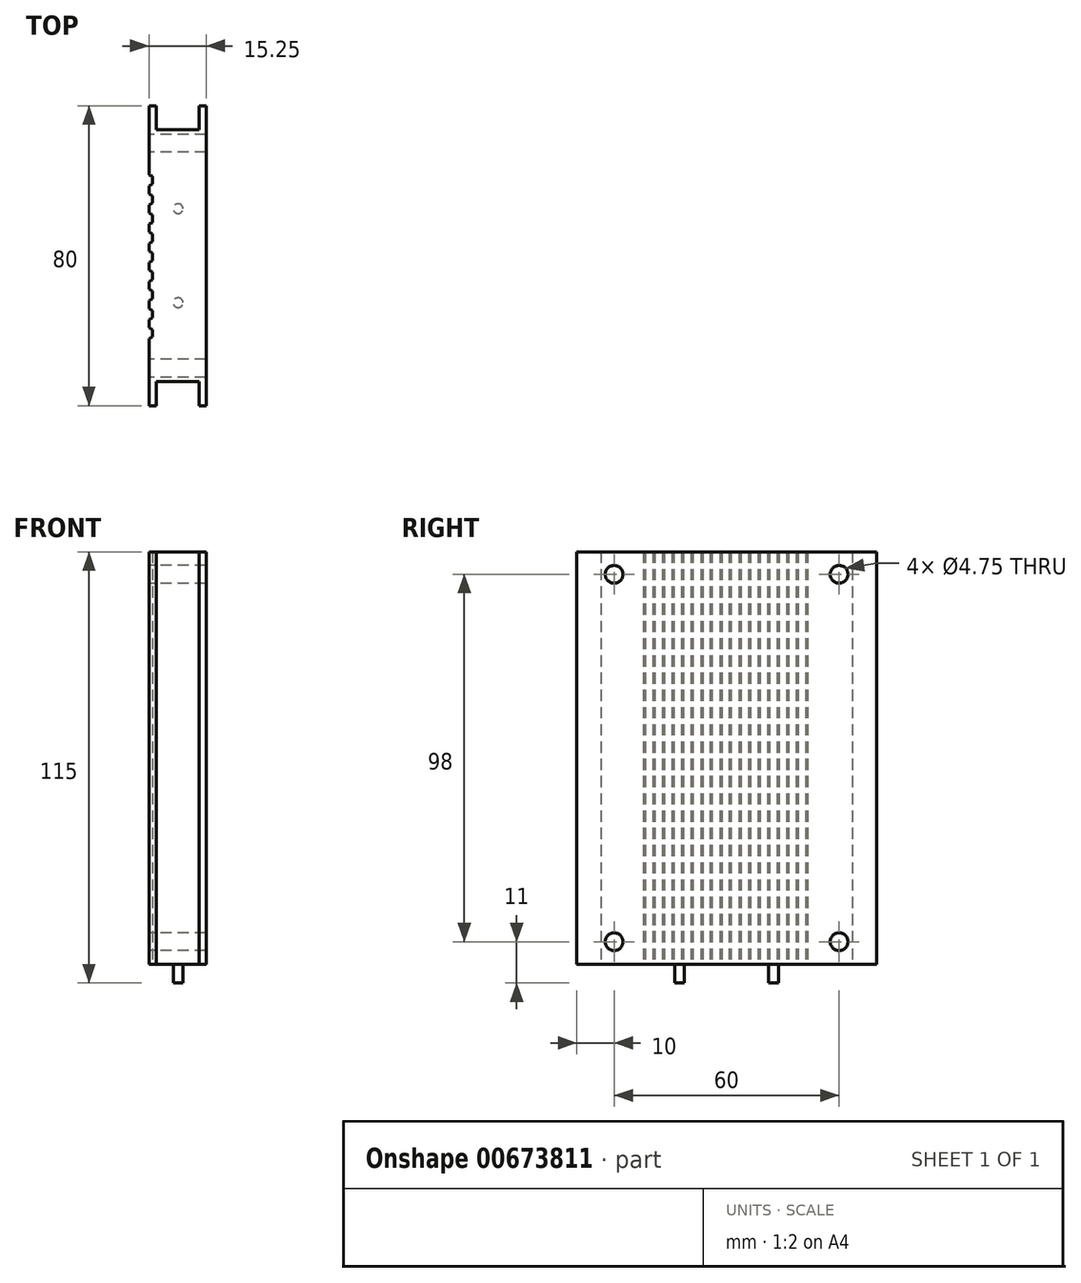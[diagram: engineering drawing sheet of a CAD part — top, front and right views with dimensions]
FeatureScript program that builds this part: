
annotation { "Feature Type Name" : "Feature", "Feature Type Description" : "" }
export const myFeature = defineFeature(function(context is Context, id is Id, definition is map)
    precondition{}
    {
        {
            var Q0;
            Q0=qCreatedBy(makeId("Top.planeOp"),FACE);
            var sketch = newSketch(context, id + "F0", { "sketchPlane" : qUnion([Q0])});
            skLineSegment(sketch, "E0", {"start": v(0, 0) * mm, "end": v(0, 80) * mm});
            skLineSegment(sketch, "E1", {"start": v(0, 80) * mm, "end": v(1.9, 80) * mm});
            skLineSegment(sketch, "E2", {"start": v(1.9, 80) * mm, "end": v(1.9, 73.55) * mm});
            skLineSegment(sketch, "E3", {"start": v(1.9, 73.55) * mm, "end": v(13.35, 73.55) * mm});
            skLineSegment(sketch, "E4", {"start": v(13.35, 73.55) * mm, "end": v(13.35, 80) * mm});
            skLineSegment(sketch, "E5", {"start": v(13.35, 80) * mm, "end": v(15.25, 80) * mm});
            skLineSegment(sketch, "E6", {"start": v(15.25, 80) * mm, "end": v(15.25, 0) * mm});
            skLineSegment(sketch, "E7", {"start": v(15.25, 0) * mm, "end": v(13.35, 0) * mm});
            skLineSegment(sketch, "E8", {"start": v(13.35, 0) * mm, "end": v(13.35, 6.45) * mm});
            skLineSegment(sketch, "E9", {"start": v(13.35, 6.45) * mm, "end": v(1.9, 6.45) * mm});
            skLineSegment(sketch, "E10", {"start": v(1.9, 6.45) * mm, "end": v(1.9, 0) * mm});
            skLineSegment(sketch, "E11", {"start": v(1.9, 0) * mm, "end": v(0, 0) * mm});
            skPoint(sketch, "E12", {"position": v(0, 61.6) * mm});
            skLineSegment(sketch, "E13", {"start": v(0, 61.6) * mm, "end": v(1, 61.1) * mm});
            skLineSegment(sketch, "E14", {"start": v(1, 61.1) * mm, "end": v(1, 59.1) * mm});
            skLineSegment(sketch, "E15", {"start": v(1, 59.1) * mm, "end": v(0, 58.6) * mm});
            skLineSegment(sketch, "E16", {"start": v(0, 58.6) * mm, "end": v(0, 61.6) * mm});
            skLineSegment(sketch, "E17.0.1.0", {"start": v(0, 56.5) * mm, "end": v(1, 56) * mm});
            skPoint(sketch, "E17.0.1.1", {"position": v(0, 56.5) * mm});
            skLineSegment(sketch, "E17.0.1.2", {"start": v(0, 53.5) * mm, "end": v(0, 56.5) * mm});
            skLineSegment(sketch, "E17.0.1.3", {"start": v(1, 54) * mm, "end": v(0, 53.5) * mm});
            skLineSegment(sketch, "E17.0.1.4", {"start": v(1, 56) * mm, "end": v(1, 54) * mm});
            skLineSegment(sketch, "E17.0.2.0", {"start": v(0, 51.4) * mm, "end": v(1, 50.9) * mm});
            skPoint(sketch, "E17.0.2.1", {"position": v(0, 51.4) * mm});
            skLineSegment(sketch, "E17.0.2.2", {"start": v(0, 48.4) * mm, "end": v(0, 51.4) * mm});
            skLineSegment(sketch, "E17.0.2.3", {"start": v(1, 48.9) * mm, "end": v(0, 48.4) * mm});
            skLineSegment(sketch, "E17.0.2.4", {"start": v(1, 50.9) * mm, "end": v(1, 48.9) * mm});
            skLineSegment(sketch, "E17.0.3.0", {"start": v(0, 46.3) * mm, "end": v(1, 45.8) * mm});
            skPoint(sketch, "E17.0.3.1", {"position": v(0, 46.3) * mm});
            skLineSegment(sketch, "E17.0.3.2", {"start": v(0, 43.3) * mm, "end": v(0, 46.3) * mm});
            skLineSegment(sketch, "E17.0.3.3", {"start": v(1, 43.8) * mm, "end": v(0, 43.3) * mm});
            skLineSegment(sketch, "E17.0.3.4", {"start": v(1, 45.8) * mm, "end": v(1, 43.8) * mm});
            skLineSegment(sketch, "E17.0.4.0", {"start": v(0, 41.2) * mm, "end": v(1, 40.7) * mm});
            skPoint(sketch, "E17.0.4.1", {"position": v(0, 41.2) * mm});
            skLineSegment(sketch, "E17.0.4.2", {"start": v(0, 38.2) * mm, "end": v(0, 41.2) * mm});
            skLineSegment(sketch, "E17.0.4.3", {"start": v(1, 38.7) * mm, "end": v(0, 38.2) * mm});
            skLineSegment(sketch, "E17.0.4.4", {"start": v(1, 40.7) * mm, "end": v(1, 38.7) * mm});
            skLineSegment(sketch, "E17.0.5.0", {"start": v(0, 36.1) * mm, "end": v(1, 35.6) * mm});
            skPoint(sketch, "E17.0.5.1", {"position": v(0, 36.1) * mm});
            skLineSegment(sketch, "E17.0.5.2", {"start": v(0, 33.1) * mm, "end": v(0, 36.1) * mm});
            skLineSegment(sketch, "E17.0.5.3", {"start": v(1, 33.6) * mm, "end": v(0, 33.1) * mm});
            skLineSegment(sketch, "E17.0.5.4", {"start": v(1, 35.6) * mm, "end": v(1, 33.6) * mm});
            skLineSegment(sketch, "E17.0.6.0", {"start": v(0, 31) * mm, "end": v(1, 30.5) * mm});
            skPoint(sketch, "E17.0.6.1", {"position": v(0, 31) * mm});
            skLineSegment(sketch, "E17.0.6.2", {"start": v(0, 28) * mm, "end": v(0, 31) * mm});
            skLineSegment(sketch, "E17.0.6.3", {"start": v(1, 28.5) * mm, "end": v(0, 28) * mm});
            skLineSegment(sketch, "E17.0.6.4", {"start": v(1, 30.5) * mm, "end": v(1, 28.5) * mm});
            skLineSegment(sketch, "E17.0.7.0", {"start": v(0, 25.9) * mm, "end": v(1, 25.4) * mm});
            skPoint(sketch, "E17.0.7.1", {"position": v(0, 25.9) * mm});
            skLineSegment(sketch, "E17.0.7.2", {"start": v(0, 22.9) * mm, "end": v(0, 25.9) * mm});
            skLineSegment(sketch, "E17.0.7.3", {"start": v(1, 23.4) * mm, "end": v(0, 22.9) * mm});
            skLineSegment(sketch, "E17.0.7.4", {"start": v(1, 25.4) * mm, "end": v(1, 23.4) * mm});
            skLineSegment(sketch, "E17.0.8.0", {"start": v(0, 20.8) * mm, "end": v(1, 20.3) * mm});
            skPoint(sketch, "E17.0.8.1", {"position": v(0, 20.8) * mm});
            skLineSegment(sketch, "E17.0.8.2", {"start": v(0, 17.8) * mm, "end": v(0, 20.8) * mm});
            skLineSegment(sketch, "E17.0.8.3", {"start": v(1, 18.3) * mm, "end": v(0, 17.8) * mm});
            skLineSegment(sketch, "E17.0.8.4", {"start": v(1, 20.3) * mm, "end": v(1, 18.3) * mm});
            skLineSegment(sketch, "E17.direction1", {"start": v(0, 58.6) * mm, "end": v(25, 58.6) * mm, "construction": true});
            skLineSegment(sketch, "E17.direction2", {"start": v(0, 58.6) * mm, "end": v(0, 53.5) * mm, "construction": true});
            skSolve(sketch);
        }
        {
            var Q0;
            {var subQ3=sQuery(id+"F0.wireOp",EDGE,"E1");Q0=makeQuery(id+"F0.imprint","IMPRINT",FACE,{"disambiguationData":[TD([[makeQuery(id+"F0.imprint","IMPRINT",EDGE,{"derivedFrom":subQ3}),-1.0]])]});}
            extrude(context, id + "F1", {"entities" : qUnion([Q0]), "depth" : 110 * mm, "offsetDistance" : 25 * mm});
        }
        {
            var Q0;
            {var subQ0=sQuery(id+"F0.wireOp",EDGE,"E0");Q0=makeQuery(id+"F1.opExtrude","SWEPT_FACE",FACE,{"disambiguationData":[OSD([subQ0]),TDD([makeQuery(id+"F0.imprint","IMPRINT",EDGE,{"disambiguationData":[TD([[makeQuery(id+"F0.imprint","INTERSECT",VERTEX,{"derivedFrom":[subQ0,sQuery(id+"F0.wireOp",EDGE,"E1")]}),1.0]])],"derivedFrom":subQ0})])]});}
            var sketch = newSketch(context, id + "F2", { "sketchPlane" : qUnion([Q0])});
            skCircle(sketch, "E18", {"center": v(-70, 6) * mm, "radius": 2.38 * mm});
            skCircle(sketch, "E19", {"center": v(-10, 6) * mm, "radius": 2.38 * mm});
            skCircle(sketch, "E20", {"center": v(-70, 104) * mm, "radius": 2.38 * mm});
            skCircle(sketch, "E21", {"center": v(-10, 104) * mm, "radius": 2.38 * mm});
            skSolve(sketch);
        }
        {
            var Q0;
            Q0=qSketchRegion(id+"F2",true);
            extrude(context, id + "F3", {"entities" : qUnion([Q0]), "operationType" : NewBodyOperationType.REMOVE, "endBound" : BoundingType.THROUGH_ALL, "oppositeDirection" : true, "depth" : 25 * mm, "offsetDistance" : 25 * mm});
        }
        {
            var Q0;
            Q0=makeQuery(id+"F1.opExtrude","CAP_FACE",FACE,{"disambiguationData":[OSD([sQuery(id+"F0.wireOp",EDGE,"E0"),sQuery(id+"F0.wireOp",EDGE,"E1"),sQuery(id+"F0.wireOp",EDGE,"E2"),sQuery(id+"F0.wireOp",EDGE,"E3"),sQuery(id+"F0.wireOp",EDGE,"E4"),sQuery(id+"F0.wireOp",EDGE,"E5"),sQuery(id+"F0.wireOp",EDGE,"E6"),sQuery(id+"F0.wireOp",EDGE,"E7"),sQuery(id+"F0.wireOp",EDGE,"E8"),sQuery(id+"F0.wireOp",EDGE,"E9"),sQuery(id+"F0.wireOp",EDGE,"E10"),sQuery(id+"F0.wireOp",EDGE,"E11"),sQuery(id+"F0.wireOp",EDGE,"E13"),sQuery(id+"F0.wireOp",EDGE,"E14"),sQuery(id+"F0.wireOp",EDGE,"E15"),sQuery(id+"F0.wireOp",EDGE,"E17.0.1.0"),sQuery(id+"F0.wireOp",EDGE,"E17.0.1.3"),sQuery(id+"F0.wireOp",EDGE,"E17.0.1.4"),sQuery(id+"F0.wireOp",EDGE,"E17.0.2.0"),sQuery(id+"F0.wireOp",EDGE,"E17.0.2.3"),sQuery(id+"F0.wireOp",EDGE,"E17.0.2.4"),sQuery(id+"F0.wireOp",EDGE,"E17.0.3.0"),sQuery(id+"F0.wireOp",EDGE,"E17.0.3.3"),sQuery(id+"F0.wireOp",EDGE,"E17.0.3.4"),sQuery(id+"F0.wireOp",EDGE,"E17.0.4.0"),sQuery(id+"F0.wireOp",EDGE,"E17.0.4.3"),sQuery(id+"F0.wireOp",EDGE,"E17.0.4.4"),sQuery(id+"F0.wireOp",EDGE,"E17.0.5.0"),sQuery(id+"F0.wireOp",EDGE,"E17.0.5.3"),sQuery(id+"F0.wireOp",EDGE,"E17.0.5.4"),sQuery(id+"F0.wireOp",EDGE,"E17.0.6.0"),sQuery(id+"F0.wireOp",EDGE,"E17.0.6.3"),sQuery(id+"F0.wireOp",EDGE,"E17.0.6.4"),sQuery(id+"F0.wireOp",EDGE,"E17.0.7.0"),sQuery(id+"F0.wireOp",EDGE,"E17.0.7.3"),sQuery(id+"F0.wireOp",EDGE,"E17.0.7.4"),sQuery(id+"F0.wireOp",EDGE,"E17.0.8.0"),sQuery(id+"F0.wireOp",EDGE,"E17.0.8.3"),sQuery(id+"F0.wireOp",EDGE,"E17.0.8.4")])],"isStart":true});
            var sketch = newSketch(context, id + "F4", { "sketchPlane" : qUnion([Q0])});
            skCircle(sketch, "E22", {"center": v(7.79, -52.55) * mm, "radius": 1.3 * mm});
            skCircle(sketch, "E23", {"center": v(7.79, -27.45) * mm, "radius": 1.3 * mm});
            skSolve(sketch);
        }
        {
            var Q0;
            Q0=makeQuery(id+"F4.imprint","IMPRINT",FACE,{"disambiguationData":[TD([[makeQuery(id+"F4.imprint","IMPRINT",EDGE,{"derivedFrom":sQuery(id+"F4.wireOp",EDGE,"E23")}),1.0]])]});
            extrude(context, id + "F5", {"entities" : qUnion([Q0]), "depth" : 5 * mm, "offsetDistance" : 25 * mm});
        }
        {
            var Q0;
            Q0=makeQuery(id+"F4.imprint","IMPRINT",FACE,{"disambiguationData":[TD([[makeQuery(id+"F4.imprint","IMPRINT",EDGE,{"derivedFrom":sQuery(id+"F4.wireOp",EDGE,"E22")}),1.0]])]});
            extrude(context, id + "F6", {"entities" : qUnion([Q0]), "depth" : 5 * mm, "offsetDistance" : 25 * mm});
        }
    });
